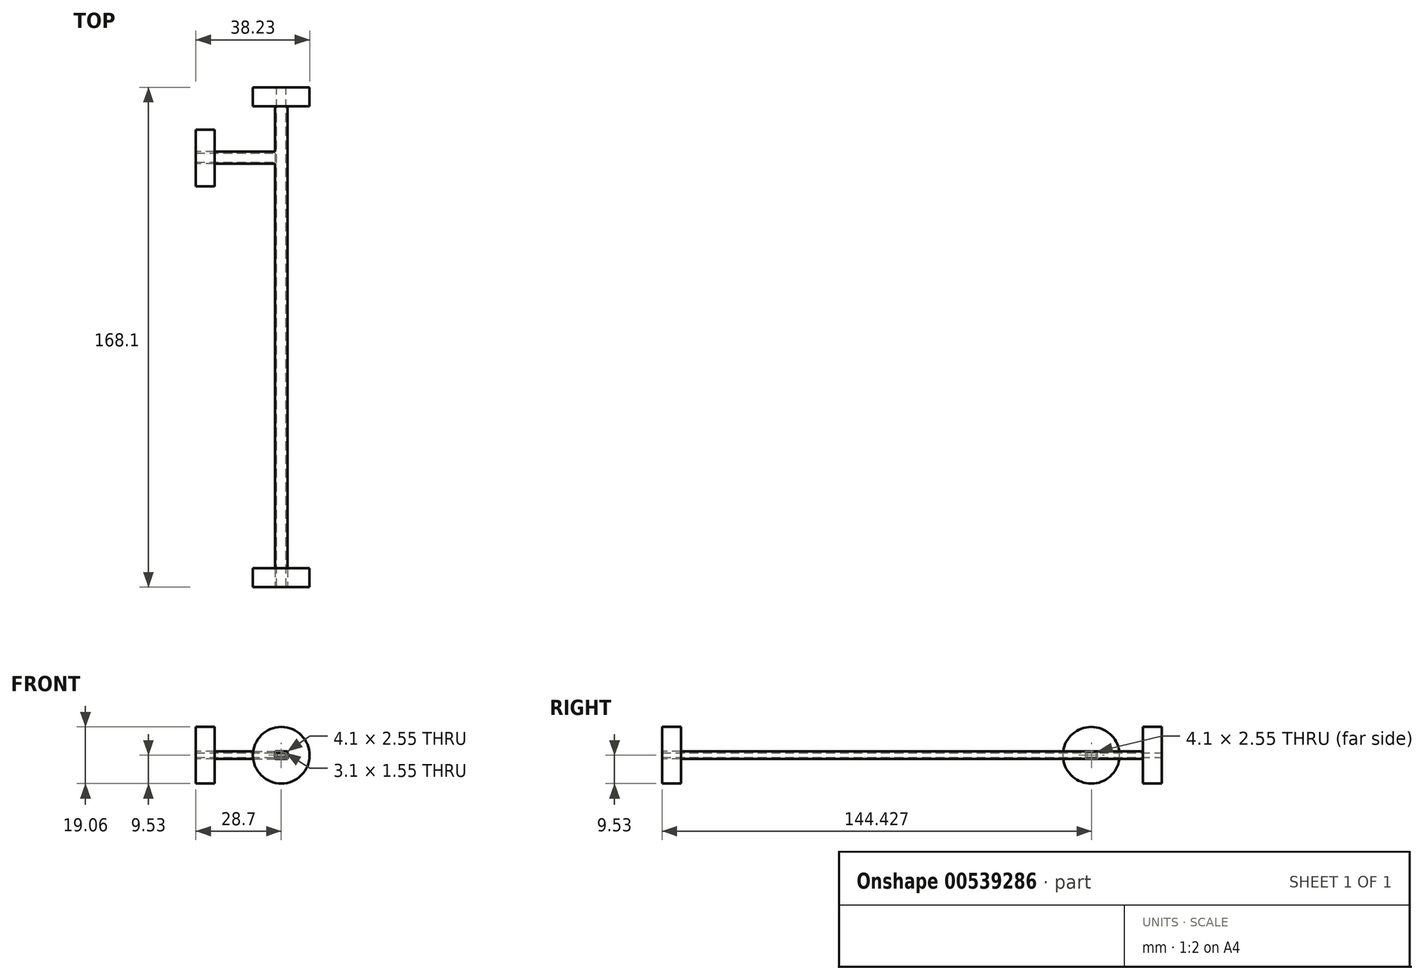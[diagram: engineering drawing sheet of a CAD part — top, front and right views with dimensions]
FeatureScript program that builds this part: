
annotation { "Feature Type Name" : "Feature", "Feature Type Description" : "" }
export const myFeature = defineFeature(function(context is Context, id is Id, definition is map)
    precondition{}
    {
        {
            var Q0;
            Q0=qCreatedBy(makeId("Front.planeOp"),FACE);
            var sketch = newSketch(context, id + "F0", { "sketchPlane" : qUnion([Q0])});
            skLineSegment(sketch, "E0.bottom", {"start": v(-1.55, 0.77) * mm, "end": v(1.55, 0.77) * mm});
            skLineSegment(sketch, "E0.top", {"start": v(-1.55, -0.77) * mm, "end": v(1.55, -0.77) * mm});
            skLineSegment(sketch, "E0.left", {"start": v(-1.55, 0.77) * mm, "end": v(-1.55, -0.77) * mm});
            skLineSegment(sketch, "E0.right", {"start": v(1.55, 0.77) * mm, "end": v(1.55, -0.77) * mm});
            skPoint(sketch, "E0.middle", {"position": v(0, 0) * mm});
            skLineSegment(sketch, "E1.bottom", {"start": v(-2.05, -1.28) * mm, "end": v(2.05, -1.28) * mm});
            skLineSegment(sketch, "E1.top", {"start": v(-2.05, 1.28) * mm, "end": v(2.05, 1.28) * mm});
            skLineSegment(sketch, "E1.left", {"start": v(-2.05, -1.28) * mm, "end": v(-2.05, 1.28) * mm});
            skLineSegment(sketch, "E1.right", {"start": v(2.05, -1.28) * mm, "end": v(2.05, 1.28) * mm});
            skCircle(sketch, "E2", {"center": v(0, 0) * mm, "radius": 9.53 * mm});
            skSolve(sketch);
        }
        {
            assignVariable(context, id + "F1", {"name" : "Length", "anyValue" : 168.1});
        }
        {
            var Q0;
            Q0=makeQuery(id+"F0.imprint","IMPRINT",FACE,{"disambiguationData":[TD([[makeQuery(id+"F0.imprint","IMPRINT",EDGE,{"derivedFrom":sQuery(id+"F0.wireOp",EDGE,"E0.bottom")}),1.0]])]});
            extrude(context, id + "F2", {"entities" : qUnion([Q0]), "depth" : getVariable(context, 'Length') * mm, "offsetDistance" : 25 * mm});
        }
        {
            var Q0;
            Q0=makeQuery(id+"F0.imprint","IMPRINT",FACE,{"disambiguationData":[TD([[makeQuery(id+"F0.imprint","IMPRINT",EDGE,{"derivedFrom":sQuery(id+"F0.wireOp",EDGE,"E1.bottom")}),-1.0]])]});
            extrude(context, id + "F3", {"entities" : qUnion([Q0]), "operationType" : NewBodyOperationType.ADD, "depth" : 6.35 * mm, "offsetDistance" : 25 * mm});
        }
        {
            var Q0;
            Q0=makeQuery(id+"F2.opExtrude","CAP_FACE",FACE,{"disambiguationData":[OSD([sQuery(id+"F0.wireOp",EDGE,"E0.bottom"),sQuery(id+"F0.wireOp",EDGE,"E0.top"),sQuery(id+"F0.wireOp",EDGE,"E0.left"),sQuery(id+"F0.wireOp",EDGE,"E0.right"),sQuery(id+"F0.wireOp",EDGE,"E1.bottom"),sQuery(id+"F0.wireOp",EDGE,"E1.top"),sQuery(id+"F0.wireOp",EDGE,"E1.left"),sQuery(id+"F0.wireOp",EDGE,"E1.right")])],"isStart":false});
            var sketch = newSketch(context, id + "F4", { "sketchPlane" : qUnion([Q0])});
            skCircle(sketch, "E3", {"center": v(0, 0) * mm, "radius": 9.53 * mm});
            skSolve(sketch);
        }
        {
            var Q0;
            Q0=makeQuery(id+"F4.imprint","IMPRINT",FACE,{"disambiguationData":[TD([[makeQuery(id+"F4.imprint","IMPRINT",EDGE,{"derivedFrom":sQuery(id+"F4.wireOp",EDGE,"E3")}),1.0]])]});
            extrude(context, id + "F5", {"entities" : qUnion([Q0]), "oppositeDirection" : true, "depth" : 6.35 * mm, "offsetDistance" : 25 * mm});
        }
        {
            var Q0;
            Q0=qCreatedBy(makeId("Right.planeOp"),FACE);
            cPlane(context, id + "F6", {"entities" : qUnion([Q0]), "cplaneType" : CPlaneType.OFFSET, "offset" : 4.1 / 2 * mm, "oppositeDirection" : true, "width" : 150 * mm, "height" : 150 * mm});
        }
        {
            var Q0;
            Q0=qCreatedBy(id+"F6.planeOp",FACE);
            var sketch = newSketch(context, id + "F7", { "sketchPlane" : qUnion([Q0])});
            skLineSegment(sketch, "E4.bottom", {"start": v(-22.12, 0.77) * mm, "end": v(-25.22, 0.77) * mm});
            skLineSegment(sketch, "E4.top", {"start": v(-22.12, -0.78) * mm, "end": v(-25.22, -0.78) * mm});
            skLineSegment(sketch, "E4.left", {"start": v(-22.12, 0.77) * mm, "end": v(-22.12, -0.78) * mm});
            skLineSegment(sketch, "E4.right", {"start": v(-25.22, 0.77) * mm, "end": v(-25.22, -0.78) * mm});
            skPoint(sketch, "E4.middle", {"position": v(-23.67, 0) * mm});
            skLineSegment(sketch, "E5.bottom", {"start": v(-25.72, -1.27) * mm, "end": v(-21.62, -1.27) * mm});
            skLineSegment(sketch, "E5.top", {"start": v(-25.72, 1.28) * mm, "end": v(-21.62, 1.28) * mm});
            skLineSegment(sketch, "E5.left", {"start": v(-25.72, -1.27) * mm, "end": v(-25.72, 1.28) * mm});
            skLineSegment(sketch, "E5.right", {"start": v(-21.62, -1.27) * mm, "end": v(-21.62, 1.28) * mm});
            skSolve(sketch);
        }
        {
            var Q0;
            Q0=makeQuery(id+"F7.imprint","IMPRINT",FACE,{"disambiguationData":[TD([[makeQuery(id+"F7.imprint","IMPRINT",EDGE,{"derivedFrom":sQuery(id+"F7.wireOp",EDGE,"E4.bottom")}),-1.0]])]});
            extrude(context, id + "F8", {"entities" : qUnion([Q0]), "operationType" : NewBodyOperationType.ADD, "oppositeDirection" : true, "depth" : 26.65 * mm, "offsetDistance" : 25 * mm});
        }
        {
            var Q0;
            Q0=makeQuery(id+"F8.opExtrude","CAP_FACE",FACE,{"disambiguationData":[OSD([sQuery(id+"F7.wireOp",EDGE,"E4.bottom"),sQuery(id+"F7.wireOp",EDGE,"E4.top"),sQuery(id+"F7.wireOp",EDGE,"E4.left"),sQuery(id+"F7.wireOp",EDGE,"E4.right"),sQuery(id+"F7.wireOp",EDGE,"E5.bottom"),sQuery(id+"F7.wireOp",EDGE,"E5.top"),sQuery(id+"F7.wireOp",EDGE,"E5.left"),sQuery(id+"F7.wireOp",EDGE,"E5.right")])],"isStart":false});
            var sketch = newSketch(context, id + "F9", { "sketchPlane" : qUnion([Q0])});
            skCircle(sketch, "E6", {"center": v(23.75, 0) * mm, "radius": 9.53 * mm});
            skSolve(sketch);
        }
        {
            var Q0;
            Q0=makeQuery(id+"F9.imprint","IMPRINT",FACE,{"disambiguationData":[TD([[makeQuery(id+"F9.imprint","IMPRINT",EDGE,{"derivedFrom":sQuery(id+"F9.wireOp",EDGE,"E6")}),1.0]])]});
            extrude(context, id + "F10", {"entities" : qUnion([Q0]), "oppositeDirection" : true, "depth" : 6.35 * mm, "offsetDistance" : 25 * mm});
        }
    });
